# Revit family: Chair-Multi_Purpose-Allermuir-Jacier
name_source: partatom
category: Furniture
revit_build: Autodesk Revit MEP 2012 (Build: 20110309_2315)
units: mm (PartAtom-declared; Revit-internal decimal feet)

## types (2) — shared parameters
04 CSI = 12 51 00
95 CSI = 12510
Arms Height = 2' - 2"
Assembly Code = E2020200
Base = Metal - Allermuir - Upholstery - Stainless - Brushed
Chair Seat = Plastic - Allermuir - Smooth - Dark Gray
Color Availability = See price list for material options
Cushion Material = Plastic - Allermuir - Smooth - Dark Gray 2
Description = Side chair, plastic seat and back, no arms
Fabric Spec Sheets = http://www.allermuir.net
Glides = Plastic - Allermuir - Smooth - Coarse Textured - Black
Manufacturer = Allermuir
Manufacturer Fax = (419) 887 5805
Overall Depth = 1' - 8"
Overall Width = 1' - 10 1/2"
Plastic Arms in Black = No
Plugin Data URL = http://products.ecoscorecard.com
Product Line = Jacier
Seat Depth = 1' - 6"
Seat Width = 1' - 5 1/2"
Seat or Top = Plastic - Allermuir - Smooth - Dark Gray
Subcategory = Multi-Purpose Line
URL = http://www.allermuir.net
Upholstered Back = No
Upholstered Seat = No
Weight = 15.0 lb
ecoScorecard Product Page = http://products.ecoscorecard.com
ecoScorecard_data = http://thesenatorgroup.ecoscorecard.com

## per-type parameters (varying)
| type | Leg Material | Overall Height | Seat 1 | Seat 2 | Seat Height |
| JCR1 | Stainless - Allermuir -  Polished Brushed | 2' - 8" | Yes | No | 1' - 6" |
| JCR2 | Metal - Allermuir - Upholstery - Stainless - Brushed | 3' - 7 1/2" | No | Yes | 2' - 7" |

note: column(s) folded — value = type name in every type: Model

## geometry (parser evidence)
native form markers: Blend x13, Sweep x1
no freeform markers — native parametric forms only
